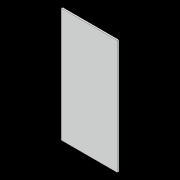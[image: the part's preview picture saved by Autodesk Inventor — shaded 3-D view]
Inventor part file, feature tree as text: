
AUTODESK INVENTOR PART (.ipt)
format: ipt  version: 2022 (Build 260153000, 153)  size: 77,824 bytes
history: native  units: in
note: dims shown in document units (in); Inventor stores cm internally (conversion verified against a paired STEP export)
features: extrude x1, sketch x1
ambient origin geometry x8: Origin, YZ Plane, XZ Plane, XY Plane, X Axis, Y Axis, Z Axis, Center Point
bodies: Solid1 (feature_tree)
feature tree (2):
  extrude  "Extrusion1"  Depth=9.6654in
  sketch  "Sketch1"  dims[d0=4.7244in d1=9.6654in d2=0.1181in d3=0.0in]
